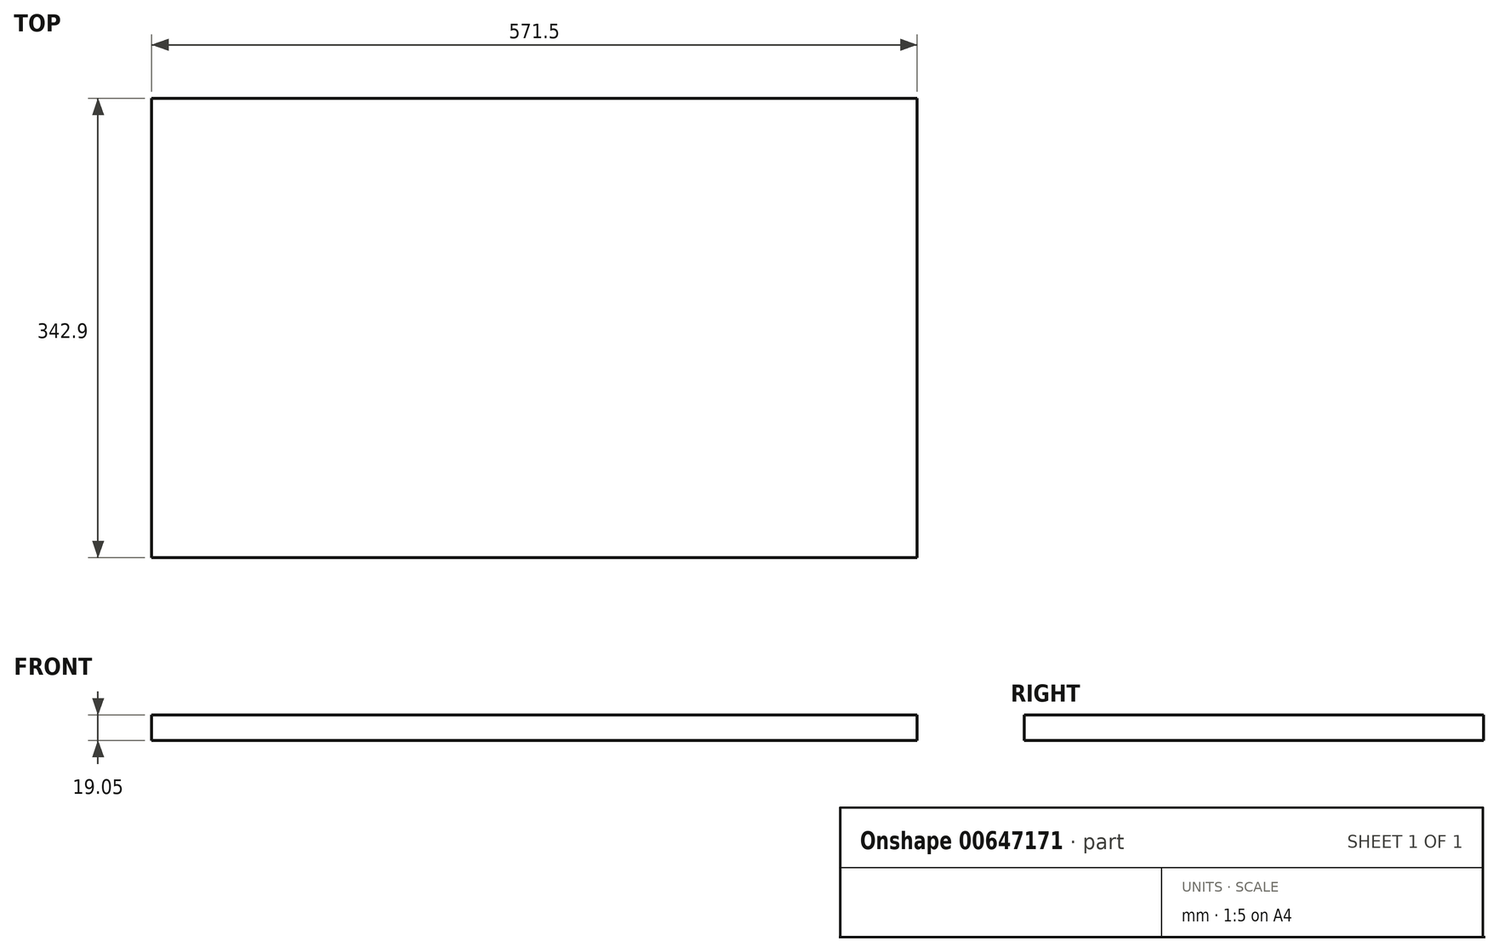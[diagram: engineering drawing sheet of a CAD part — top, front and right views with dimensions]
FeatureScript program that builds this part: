
annotation { "Feature Type Name" : "Feature", "Feature Type Description" : "" }
export const myFeature = defineFeature(function(context is Context, id is Id, definition is map)
    precondition{}
    {
        {
            var Q0;
            Q0=qCreatedBy(makeId("Top.planeOp"),FACE);
            var sketch = newSketch(context, id + "F0", { "sketchPlane" : qUnion([Q0])});
            skLineSegment(sketch, "E0.bottom", {"start": v(285.75, 171.45) * mm, "end": v(-285.75, 171.45) * mm});
            skLineSegment(sketch, "E0.top", {"start": v(285.75, -171.45) * mm, "end": v(-285.75, -171.45) * mm});
            skLineSegment(sketch, "E0.left", {"start": v(285.75, 171.45) * mm, "end": v(285.75, -171.45) * mm});
            skLineSegment(sketch, "E0.right", {"start": v(-285.75, 171.45) * mm, "end": v(-285.75, -171.45) * mm});
            skPoint(sketch, "E0.middle", {"position": v(0, 0) * mm});
            skSolve(sketch);
        }
        {
            var Q0;
            Q0=makeQuery(id+"F0.imprint","IMPRINT",FACE,{"disambiguationData":[TD([[makeQuery(id+"F0.imprint","IMPRINT",EDGE,{"derivedFrom":sQuery(id+"F0.wireOp",EDGE,"E0.bottom")}),1.0]])]});
            extrude(context, id + "F1", {"entities" : qUnion([Q0]), "depth" : 19.05 * mm, "offsetDistance" : 25.4 * mm});
        }
    });
